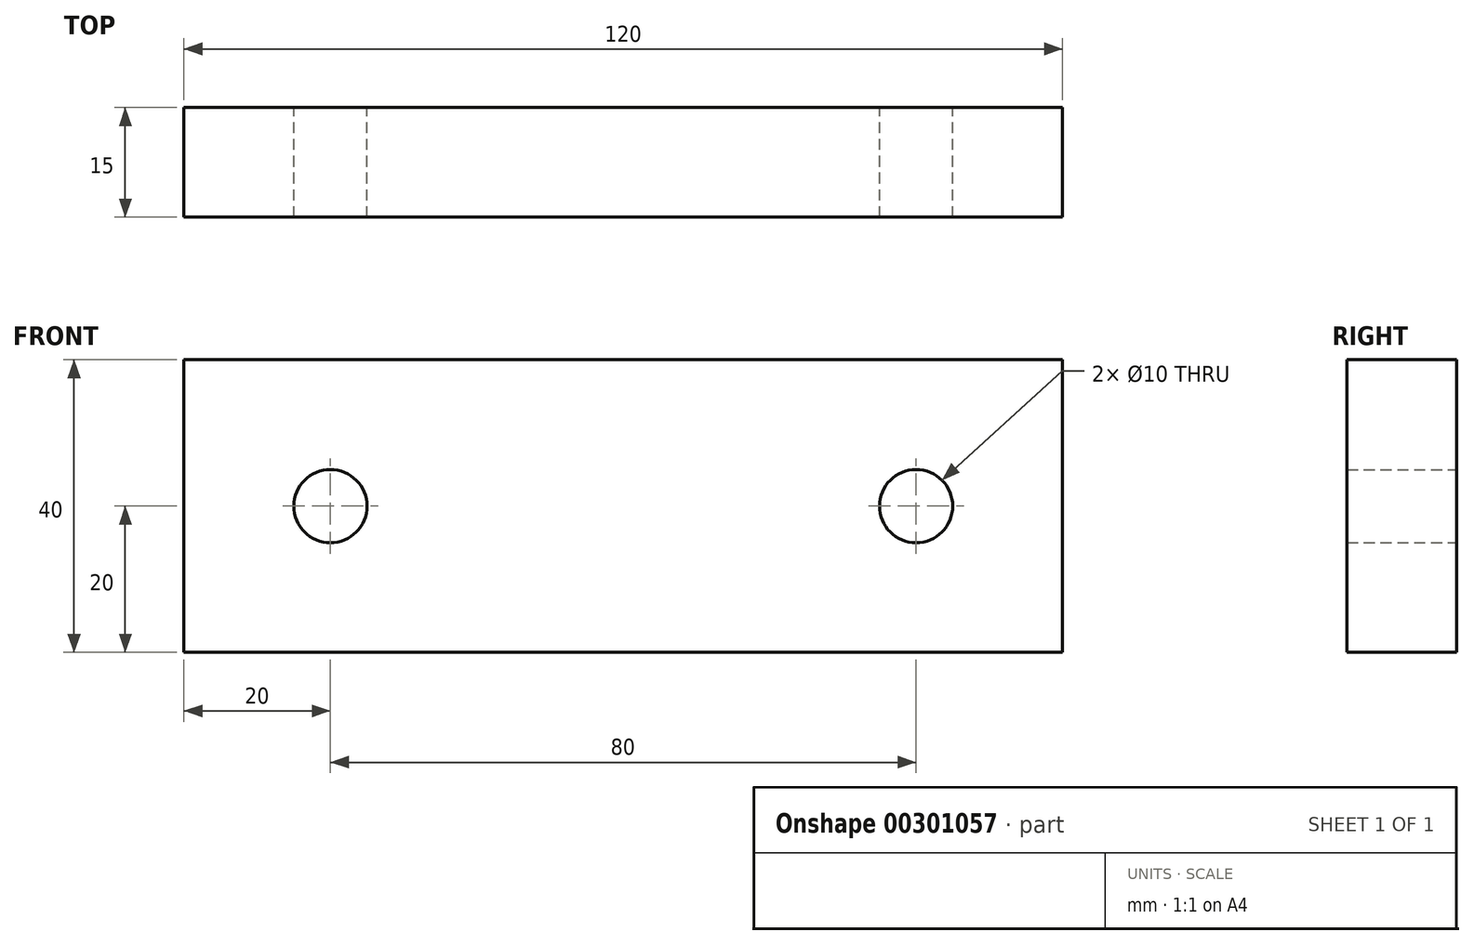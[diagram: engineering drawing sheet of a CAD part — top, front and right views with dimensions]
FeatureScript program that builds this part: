
annotation { "Feature Type Name" : "Feature", "Feature Type Description" : "" }
export const myFeature = defineFeature(function(context is Context, id is Id, definition is map)
    precondition{}
    {
        {
            var Q0;
            Q0=qCreatedBy(makeId("Front.planeOp"),FACE);
            var sketch = newSketch(context, id + "F0", { "sketchPlane" : qUnion([Q0])});
            skLineSegment(sketch, "E0.bottom", {"start": v(0, 0) * mm, "end": v(120, 0) * mm});
            skLineSegment(sketch, "E0.top", {"start": v(0, 40) * mm, "end": v(120, 40) * mm});
            skLineSegment(sketch, "E0.left", {"start": v(0, 0) * mm, "end": v(0, 40) * mm});
            skLineSegment(sketch, "E0.right", {"start": v(120, 0) * mm, "end": v(120, 40) * mm});
            skCircle(sketch, "E1", {"center": v(20, 20) * mm, "radius": 5 * mm});
            skPoint(sketch, "E1.centerSnap0", {"position": v(0, 20) * mm});
            skCircle(sketch, "E2", {"center": v(100, 20) * mm, "radius": 5 * mm});
            skSolve(sketch);
        }
        {
            var Q0;
            Q0 = qSketchRegion(id + "F0", true);
            extrude(context, id + "F1", {"entities" : qUnion([Q0]), "depth" : 15 * mm});
        }
    });
